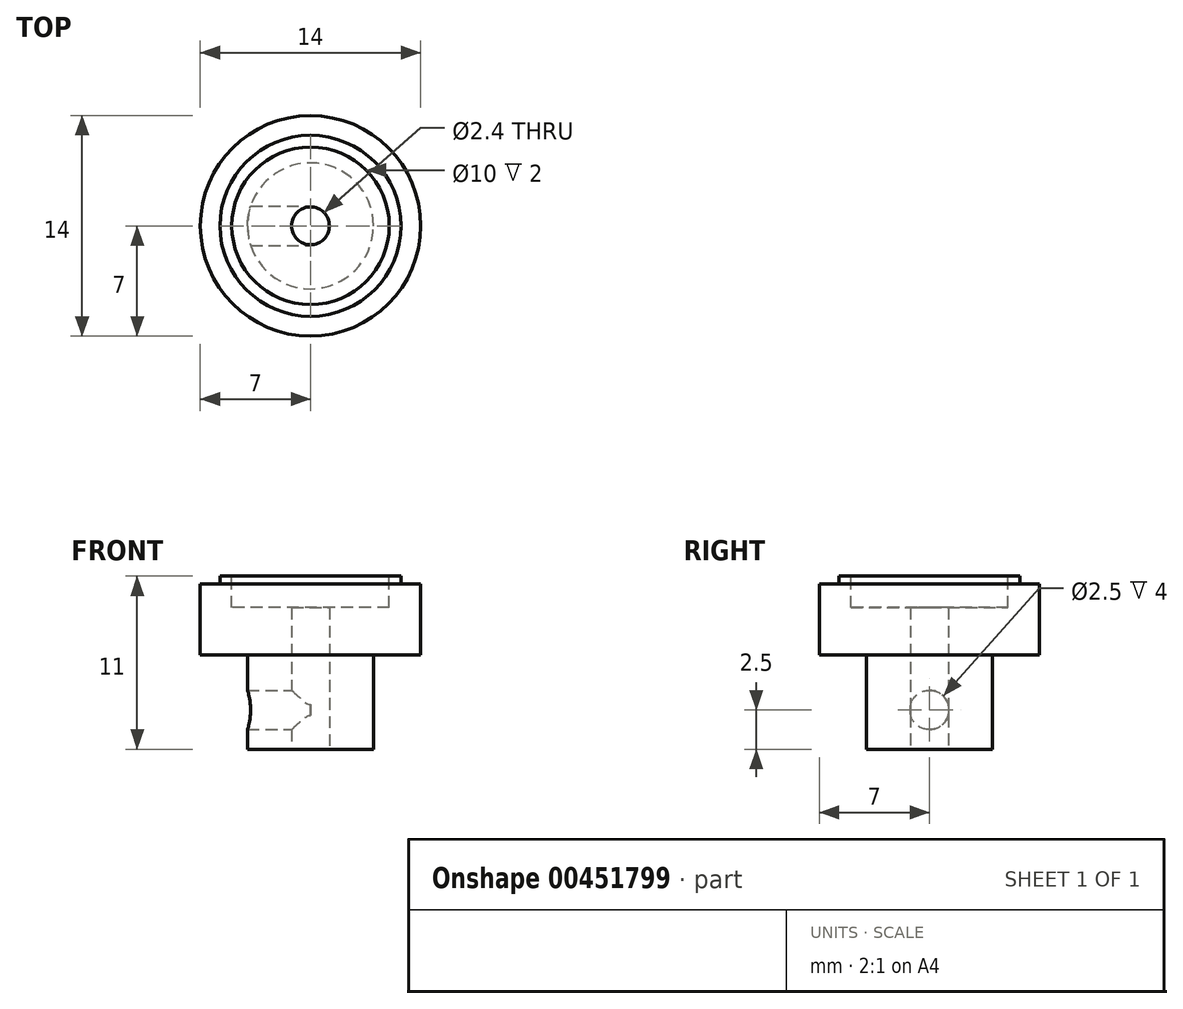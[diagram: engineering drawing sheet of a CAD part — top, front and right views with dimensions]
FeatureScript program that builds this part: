
annotation { "Feature Type Name" : "Feature", "Feature Type Description" : "" }
export const myFeature = defineFeature(function(context is Context, id is Id, definition is map)
    precondition{}
    {
        {
            var Q0;
            Q0=qCreatedBy(makeId("Top.planeOp"),FACE);
            var sketch = newSketch(context, id + "F0", { "sketchPlane" : qUnion([Q0])});
            skCircle(sketch, "E0", {"center": v(0, 0) * mm, "radius": 8 * mm});
            skSolve(sketch);
        }
        {
            var Q0;
            Q0=qSketchRegion(id+"F0",true);
            extrude(context, id + "F1", {"entities" : qUnion([Q0]), "depth" : 5 * mm});
        }
        {
            var Q0;
            Q0=makeQuery(id+"F1.opExtrude","CAP_FACE",FACE,{"disambiguationData":[OSD([sQuery(id+"F0.wireOp",EDGE,"E0")])],"isStart":true});
            var sketch = newSketch(context, id + "F2", { "sketchPlane" : qUnion([Q0])});
            skCircle(sketch, "E1", {"center": v(0, 0) * mm, "radius": 4 * mm});
            skSolve(sketch);
        }
        {
            var Q0;
            Q0=qSketchRegion(id+"F2",true);
            extrude(context, id + "F3", {"entities" : qUnion([Q0]), "operationType" : NewBodyOperationType.ADD, "depth" : 6 * mm});
        }
        {
            var Q0;
            Q0=makeQuery(id+"F3.opExtrude","CAP_FACE",FACE,{"disambiguationData":[OSD([sQuery(id+"F2.wireOp",EDGE,"E1")])],"isStart":false});
            var sketch = newSketch(context, id + "F4", { "sketchPlane" : qUnion([Q0])});
            skCircle(sketch, "E2", {"center": v(0, 0) * mm, "radius": 1.2 * mm});
            skSolve(sketch);
        }
        {
            var Q0;
            Q0=qSketchRegion(id+"F4",true);
            extrude(context, id + "F5", {"entities" : qUnion([Q0]), "operationType" : NewBodyOperationType.REMOVE, "oppositeDirection" : true, "depth" : 9 * mm});
        }
        {
            var Q0;
            Q0=makeQuery(id+"F1.opExtrude","CAP_FACE",FACE,{"disambiguationData":[OSD([sQuery(id+"F0.wireOp",EDGE,"E0")])],"isStart":false});
            var sketch = newSketch(context, id + "F6", { "sketchPlane" : qUnion([Q0])});
            skCircle(sketch, "E3", {"center": v(0, 0) * mm, "radius": 5 * mm});
            skSolve(sketch);
        }
        {
            var Q0;
            Q0=qSketchRegion(id+"F6",true);
            extrude(context, id + "F7", {"entities" : qUnion([Q0]), "operationType" : NewBodyOperationType.REMOVE, "oppositeDirection" : true, "depth" : 2 * mm});
        }
        {
            var Q0;
            Q0=makeQuery(id+"F1.opExtrude","CAP_FACE",FACE,{"disambiguationData":[OSD([sQuery(id+"F0.wireOp",EDGE,"E0")])],"isStart":false});
            var sketch = newSketch(context, id + "F8", { "sketchPlane" : qUnion([Q0])});
            skCircle(sketch, "E4", {"center": v(0, 0) * mm, "radius": 7.5 * mm});
            skCircle(sketch, "E5", {"center": v(0, 0) * mm, "radius": 6.75 * mm});
            skSolve(sketch);
        }
        {
            var Q0;
            Q0=makeQuery(id+"F8.imprint","IMPRINT",FACE,{"disambiguationData":[TD([[makeQuery(id+"F8.imprint","IMPRINT",EDGE,{"derivedFrom":sQuery(id+"F8.wireOp",EDGE,"E4")}),1.0]])]});
            extrude(context, id + "F9", {"entities" : qUnion([Q0]), "operationType" : NewBodyOperationType.REMOVE, "oppositeDirection" : true, "depth" : 0.5 * mm});
        }
        {
            var Q0;
            Q0=makeQuery(id+"F9.boolean.opBoolean","COPY",EDGE,{"derivedFrom":makeQuery(id+"F9.opExtrude","CAP_EDGE",EDGE,{"disambiguationData":[OSD([sQuery(id+"F8.wireOp",EDGE,"E5")])],"isStart":true})});
            chamfer(context, id + "F10", {"entities" : qUnion([Q0]), "width" : 0.2 * mm, "tangentPropagation" : true});
        }
        {
            var Q0;
            {var subQ0=sQuery(id+"F8.wireOp",EDGE,"E5");Q0=makeQuery(id+"F10.opChamfer","BLEND_EDGE",EDGE,{"blendedFrom":[makeQuery(id+"F9.boolean.opBoolean","COPY",EDGE,{"derivedFrom":makeQuery(id+"F9.opExtrude","CAP_EDGE",EDGE,{"disambiguationData":[OSD([subQ0])],"isStart":true})}),makeQuery(id+"F9.boolean.opBoolean","COPY",FACE,{"derivedFrom":makeQuery(id+"F9.opExtrude","SWEPT_FACE",FACE,{"disambiguationData":[OSD([subQ0])]})})],"blendedInto":[makeQuery(id+"F9.boolean.opBoolean","COPY",FACE,{"derivedFrom":makeQuery(id+"F9.opExtrude","SWEPT_FACE",FACE,{"disambiguationData":[OSD([subQ0])]})})]});}
            var Q1;
            Q1=makeQuery(id+"F5.boolean.opBoolean","COPY",EDGE,{"derivedFrom":makeQuery(id+"F5.opExtrude","CAP_EDGE",EDGE,{"disambiguationData":[OSD([sQuery(id+"F4.wireOp",EDGE,"E2")])],"isStart":false})});
            var Q2;
            Q2=makeQuery(id+"F5.boolean.opBoolean","COPY",EDGE,{"derivedFrom":makeQuery(id+"F5.opExtrude","CAP_EDGE",EDGE,{"disambiguationData":[OSD([sQuery(id+"F4.wireOp",EDGE,"E2")])],"isStart":true})});
            fillet(context, id + "F11", {"entities" : qUnion([Q0, Q1, Q2]), "radius" : 0.2 * mm, "tangentPropagation" : true, "allowEdgeOverflow" : false});
        }
        {
            var Q0;
            Q0=qCreatedBy(makeId("Top.planeOp"),FACE);
            cPlane(context, id + "F12", {"entities" : qUnion([Q0]), "cplaneType" : CPlaneType.OFFSET, "offset" : 5 * mm, "width" : 150 * mm, "height" : 150 * mm});
        }
        {
            var Q0;
            Q0=qCreatedBy(makeId("Right.planeOp"),FACE);
            var sketch = newSketch(context, id + "F13", { "sketchPlane" : qUnion([Q0])});
            skPoint(sketch, "E6", {"position": v(0, -3.5) * mm});
            skCircle(sketch, "E7", {"center": v(0, -3.5) * mm, "radius": 1.25 * mm});
            skSolve(sketch);
        }
        {
            var Q0;
            Q0=qSketchRegion(id+"F13",true);
            extrude(context, id + "F14", {"entities" : qUnion([Q0]), "operationType" : NewBodyOperationType.REMOVE, "oppositeDirection" : true, "depth" : 4.5 * mm});
        }
        {
            var Q0;
            Q0=makeQuery(id+"F9.boolean.opBoolean","SPLIT",FACE,{"disambiguationData":[TD([makeQuery(id+"F7.boolean.opBoolean","COPY",FACE,{"derivedFrom":makeQuery(id+"F7.opExtrude","SWEPT_FACE",FACE,{"disambiguationData":[OSD([sQuery(id+"F6.wireOp",EDGE,"E3")])]})})])],"derivedFrom":makeQuery(id+"F1.opExtrude","CAP_FACE",FACE,{"disambiguationData":[OSD([sQuery(id+"F0.wireOp",EDGE,"E0")])],"isStart":false})});
            var sketch = newSketch(context, id + "F15", { "sketchPlane" : qUnion([Q0])});
            skCircle(sketch, "E8", {"center": v(0, 0) * mm, "radius": 5.75 * mm});
            skCircle(sketch, "E9", {"center": v(0, 0) * mm, "radius": 7 * mm});
            skCircle(sketch, "E10", {"center": v(0, 0) * mm, "radius": 8 * mm});
            skSolve(sketch);
        }
        {
            var Q0;
            Q0=makeQuery(id+"F15.imprint","IMPRINT",FACE,{"disambiguationData":[TD([[makeQuery(id+"F15.imprint","IMPRINT",EDGE,{"derivedFrom":sQuery(id+"F15.wireOp",EDGE,"E9")}),-1.0]])]});
            extrude(context, id + "F16", {"entities" : qUnion([Q0]), "operationType" : NewBodyOperationType.REMOVE, "oppositeDirection" : true, "depth" : 10 * mm, "offsetDistance" : 25 * mm});
        }
        {
            var Q0;
            Q0=makeQuery(id+"F9.boolean.opBoolean","SPLIT",FACE,{"disambiguationData":[TD([makeQuery(id+"F7.boolean.opBoolean","COPY",FACE,{"derivedFrom":makeQuery(id+"F7.opExtrude","SWEPT_FACE",FACE,{"disambiguationData":[OSD([sQuery(id+"F6.wireOp",EDGE,"E3")])]})})])],"derivedFrom":makeQuery(id+"F1.opExtrude","CAP_FACE",FACE,{"disambiguationData":[OSD([sQuery(id+"F0.wireOp",EDGE,"E0")])],"isStart":false})});
            var sketch = newSketch(context, id + "F17", { "sketchPlane" : qUnion([Q0])});
            skCircle(sketch, "E11", {"center": v(0, 0) * mm, "radius": 5.75 * mm});
            skCircle(sketch, "E12", {"center": v(0, 0) * mm, "radius": 7 * mm});
            skSolve(sketch);
        }
        {
            var Q0;
            Q0 = qSketchRegion(id + "F17", true);
            extrude(context, id + "F18", {"entities" : qUnion([Q0]), "operationType" : NewBodyOperationType.REMOVE, "oppositeDirection" : true, "depth" : 0.5 * mm, "offsetDistance" : 25 * mm});
        }
    });
